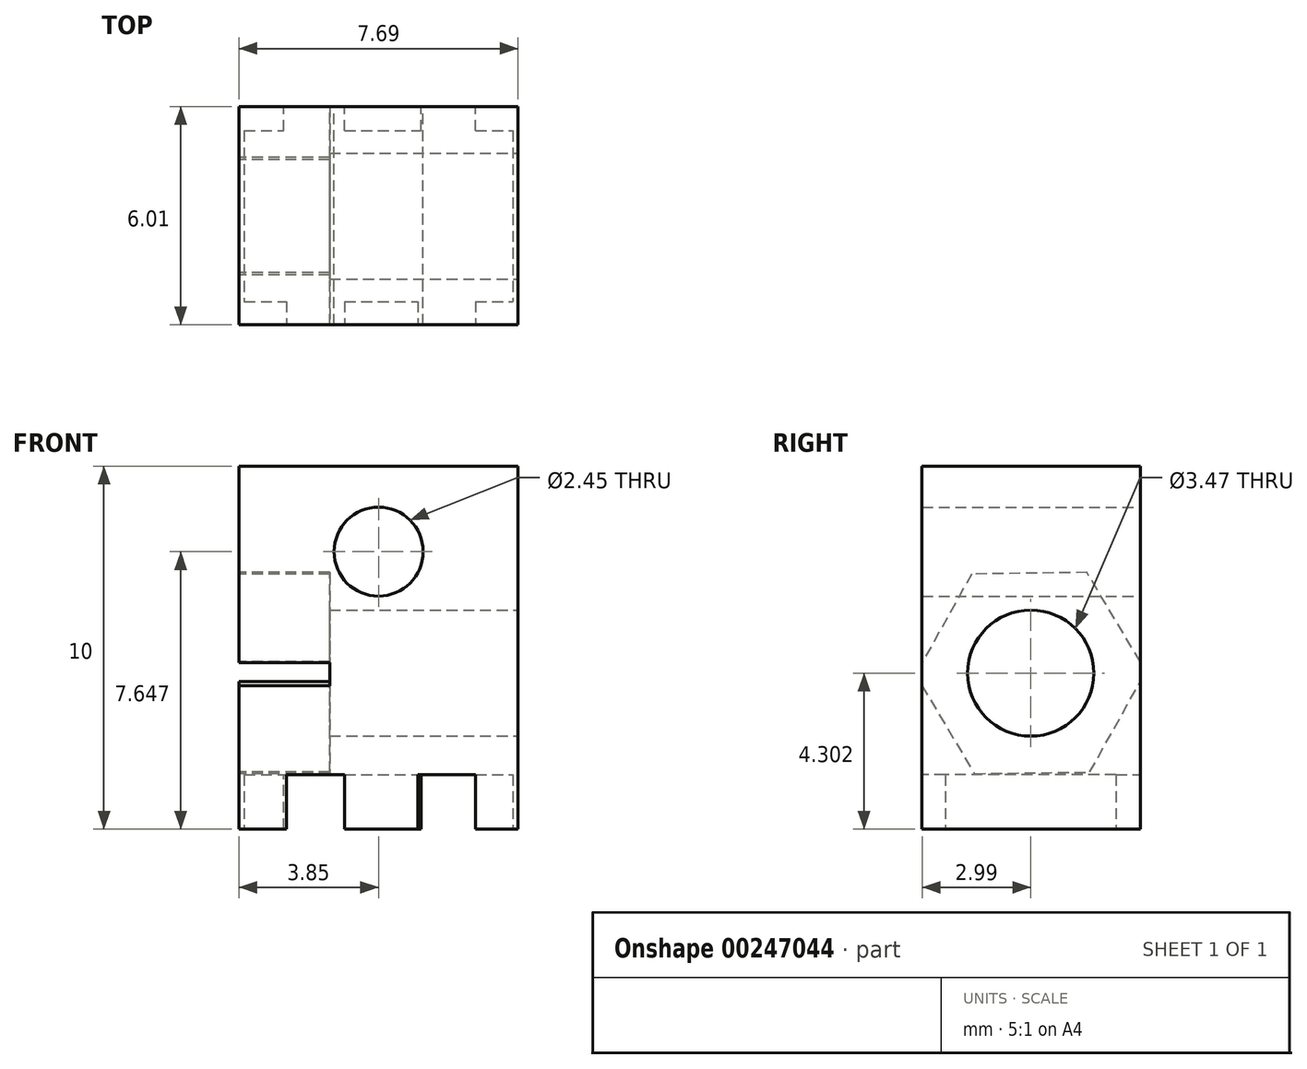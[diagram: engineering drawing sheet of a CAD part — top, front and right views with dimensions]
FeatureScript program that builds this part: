
annotation { "Feature Type Name" : "Feature", "Feature Type Description" : "" }
export const myFeature = defineFeature(function(context is Context, id is Id, definition is map)
    precondition{}
    {
        {
            var Q0;
            Q0=qCreatedBy(makeId("Top.planeOp"),FACE);
            var sketch = newSketch(context, id + "F0", { "sketchPlane" : qUnion([Q0])});
            skLineSegment(sketch, "E0.bottom", {"start": v(-3.85, 3.02) * mm, "end": v(3.84, 3.02) * mm});
            skLineSegment(sketch, "E0.top", {"start": v(-3.85, -3) * mm, "end": v(3.84, -3) * mm});
            skLineSegment(sketch, "E0.left", {"start": v(-3.85, 3.02) * mm, "end": v(-3.85, -3) * mm});
            skLineSegment(sketch, "E0.right", {"start": v(3.84, 3.02) * mm, "end": v(3.84, -3) * mm});
            skSolve(sketch);
        }
        {
            var Q0;
            Q0 = qSketchRegion(id + "F0", true);
            extrude(context, id + "F1", {"entities" : qUnion([Q0]), "depth" : 10 * mm});
        }
        {
            var Q0;
            Q0=qCreatedBy(makeId("Top.planeOp"),FACE);
            var sketch = newSketch(context, id + "F2", { "sketchPlane" : qUnion([Q0])});
            skLineSegment(sketch, "E1.bottom", {"start": v(-3.7, 2.35) * mm, "end": v(3.7, 2.35) * mm});
            skLineSegment(sketch, "E1.top", {"start": v(-3.7, -2.35) * mm, "end": v(3.7, -2.35) * mm});
            skLineSegment(sketch, "E1.left", {"start": v(-3.7, 2.35) * mm, "end": v(-3.7, -2.35) * mm});
            skLineSegment(sketch, "E1.right", {"start": v(3.7, 2.35) * mm, "end": v(3.7, -2.35) * mm});
            skLineSegment(sketch, "E2.bottom", {"start": v(-2.53, -2.35) * mm, "end": v(-0.94, -2.35) * mm});
            skLineSegment(sketch, "E2.top", {"start": v(-2.53, -3.9) * mm, "end": v(-0.94, -3.9) * mm});
            skLineSegment(sketch, "E2.left", {"start": v(-2.53, -2.35) * mm, "end": v(-2.53, -3.9) * mm});
            skLineSegment(sketch, "E2.right", {"start": v(-0.94, -2.35) * mm, "end": v(-0.94, -3.9) * mm});
            skLineSegment(sketch, "E3.bottom", {"start": v(1.08, -2.35) * mm, "end": v(2.67, -2.35) * mm});
            skLineSegment(sketch, "E3.top", {"start": v(1.08, -3.9) * mm, "end": v(2.67, -3.9) * mm});
            skLineSegment(sketch, "E3.left", {"start": v(1.08, -2.35) * mm, "end": v(1.08, -3.9) * mm});
            skLineSegment(sketch, "E3.right", {"start": v(2.67, -2.35) * mm, "end": v(2.67, -3.9) * mm});
            skLineSegment(sketch, "E4.bottom", {"start": v(-2.62, 2.35) * mm, "end": v(-0.94, 2.35) * mm});
            skLineSegment(sketch, "E4.top", {"start": v(-2.62, 3.56) * mm, "end": v(-0.94, 3.56) * mm});
            skLineSegment(sketch, "E4.left", {"start": v(-2.62, 2.35) * mm, "end": v(-2.62, 3.56) * mm});
            skLineSegment(sketch, "E4.right", {"start": v(-0.94, 2.35) * mm, "end": v(-0.94, 3.56) * mm});
            skLineSegment(sketch, "E5.bottom", {"start": v(1.17, 2.35) * mm, "end": v(2.67, 2.35) * mm});
            skLineSegment(sketch, "E5.top", {"start": v(1.17, 3.56) * mm, "end": v(2.67, 3.56) * mm});
            skLineSegment(sketch, "E5.left", {"start": v(1.17, 2.35) * mm, "end": v(1.17, 3.56) * mm});
            skLineSegment(sketch, "E5.right", {"start": v(2.67, 2.35) * mm, "end": v(2.67, 3.56) * mm});
            skSolve(sketch);
        }
        {
            var Q0;
            Q0 = qSketchRegion(id + "F2", true);
            extrude(context, id + "F3", {"entities" : qUnion([Q0]), "operationType" : NewBodyOperationType.REMOVE, "depth" : 1.5 * mm});
        }
        {
            var Q0;
            Q0=qCreatedBy(makeId("Right.planeOp"),FACE);
            var sketch = newSketch(context, id + "F4", { "sketchPlane" : qUnion([Q0])});
            skCircle(sketch, "E6", {"center": v(0, 4.3) * mm, "radius": 1.74 * mm});
            skSolve(sketch);
        }
        {
            var Q0;
            Q0 = qSketchRegion(id + "F4", true);
            extrude(context, id + "F5", {"entities" : qUnion([Q0]), "operationType" : NewBodyOperationType.REMOVE, "oppositeDirection" : true, "depth" : 25 * mm, "hasSecondDirection" : true, "secondDirectionOppositeDirection" : false, "secondDirectionDepth" : 25 * mm});
        }
        {
            var Q0;
            Q0=qCreatedBy(makeId("Front.planeOp"),FACE);
            var sketch = newSketch(context, id + "F6", { "sketchPlane" : qUnion([Q0])});
            skCircle(sketch, "E7", {"center": v(0, 7.65) * mm, "radius": 1.23 * mm});
            skSolve(sketch);
        }
        {
            var Q0;
            Q0 = qSketchRegion(id + "F6", true);
            extrude(context, id + "F7", {"entities" : qUnion([Q0]), "operationType" : NewBodyOperationType.REMOVE, "depth" : 25 * mm, "hasSecondDirection" : true, "secondDirectionOppositeDirection" : true, "secondDirectionDepth" : 25 * mm});
        }
        {
            var Q0;
            Q0=makeQuery(id+"F1.opExtrude","SWEPT_FACE",FACE,{"disambiguationData":[OSD([sQuery(id+"F0.wireOp",EDGE,"E0.left")])]});
            var sketch = newSketch(context, id + "F8", { "sketchPlane" : qUnion([Q0])});
            skCircle(sketch, "E8.cCircle", {"center": v(0, 4.3) * mm, "radius": 2.75 * mm, "construction": true});
            skLineSegment(sketch, "E8.0", {"start": v(1.62, 7.03) * mm, "end": v(3.18, 4.26) * mm});
            skLineSegment(sketch, "E8.1", {"start": v(3.18, 4.26) * mm, "end": v(1.55, 1.53) * mm});
            skLineSegment(sketch, "E8.2", {"start": v(1.55, 1.53) * mm, "end": v(-1.62, 1.57) * mm});
            skLineSegment(sketch, "E8.3", {"start": v(-1.62, 1.57) * mm, "end": v(-3.18, 4.35) * mm});
            skLineSegment(sketch, "E8.4", {"start": v(-3.18, 4.35) * mm, "end": v(-1.55, 7.07) * mm});
            skLineSegment(sketch, "E8.5", {"start": v(-1.55, 7.07) * mm, "end": v(1.62, 7.03) * mm});
            skPoint(sketch, "E8.0.midPoint", {"position": v(2.4, 5.64) * mm});
            skSolve(sketch);
        }
        {
            var Q0;
            {var subQ1=sQuery(id+"F8.wireOp",EDGE,"E8.2");Q0=makeQuery(id+"F8.imprint","IMPRINT",FACE,{"disambiguationData":[TD([[makeQuery(id+"F8.imprint","IMPRINT",EDGE,{"derivedFrom":subQ1}),-1.0]])]});}
            extrude(context, id + "F9", {"entities" : qUnion([Q0]), "operationType" : NewBodyOperationType.REMOVE, "oppositeDirection" : true, "depth" : 2.5 * mm});
        }
    });
